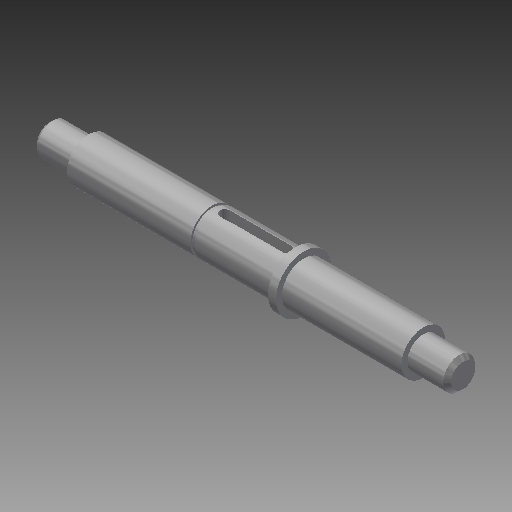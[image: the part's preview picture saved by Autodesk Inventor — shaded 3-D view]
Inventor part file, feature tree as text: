
AUTODESK INVENTOR PART (.ipt)
format: ipt  version: 2018 (Build 220112000, 112)  size: 173,056 bytes
history: native  units: mm
features: other x7, chamfer x2, revolve x1
ambient origin geometry x6: Origin, XZ Plane, XY Plane, X Axis, Y Axis, Z Axis
bodies: Solid1 (feature_tree)
feature tree (10):
  revolve  "Revolution1"  [1 undecoded]
  other  "Retaining Ring Groove3"
  chamfer  "Chamfer5"  Distance=4.0mm
  other  "Keyway3"
  chamfer  "Chamfer4"  Distance=4.0mm
  other  "Start Plane"
  other  "Origin point"
  other  "Main Sketch"
  other  "iFeature3:3"
  other  "iFeature27:3"
note: 1 required parameter value undecoded (feature->parameter linkage not recoverable at this tier; creation-order binding heuristic only, values carry confidence <= 0.55)
